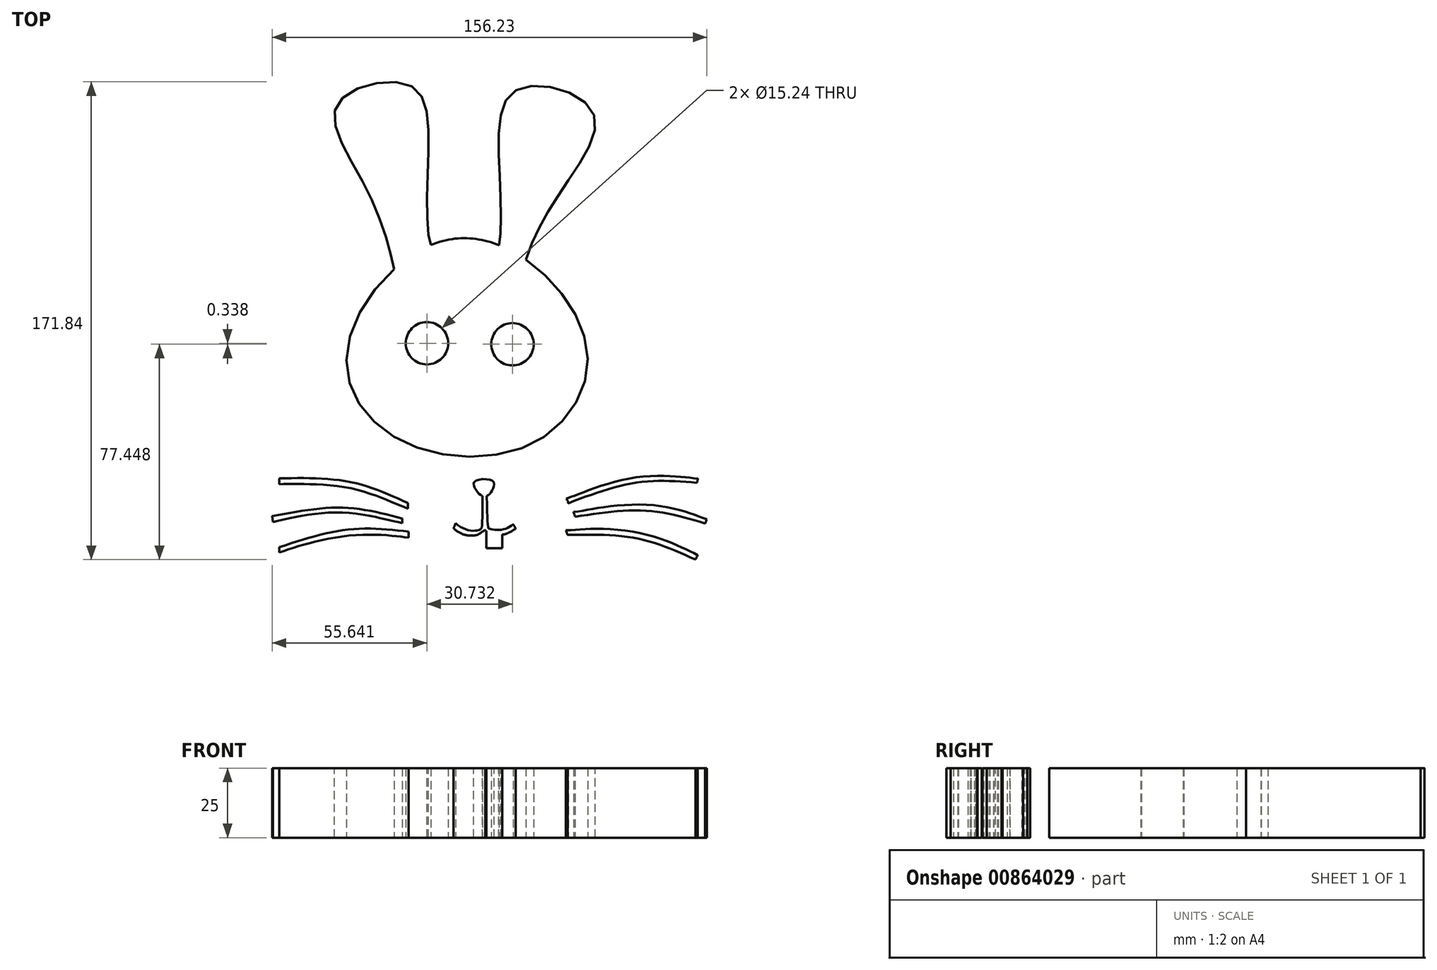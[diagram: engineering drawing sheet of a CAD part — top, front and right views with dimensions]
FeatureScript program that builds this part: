
annotation { "Feature Type Name" : "Feature", "Feature Type Description" : "" }
export const myFeature = defineFeature(function(context is Context, id is Id, definition is map)
    precondition{}
    {
        {
            var Q0;
            Q0=qCreatedBy(makeId("Top.planeOp"),FACE);
            var sketch = newSketch(context, id + "F0", { "sketchPlane" : qUnion([Q0])});
            skFitSpline(sketch, "E0", {"points": [v(-36.2, 9.29) * mm, v(12.18, 7.82) * mm, v(31.91, 39.07) * mm, v(9.73, 73.68) * mm, v(-24.49, 79.1) * mm, v(-54.7, 41.08) * mm, v(-36.2, 9.29) * mm]});
            skFitSpline(sketch, "E1", {"points": [v(-37.74, 70.4) * mm, v(-48.46, 100.88) * mm, v(-58.06, 129.69) * mm, v(-31.96, 136.42) * mm, v(-25.5, 110.88) * mm, v(-24.49, 79.1) * mm], "startDerivative": vector(-22.6, 116.84) * mm, "endDerivative": vector(28.19, -55.26) * mm});
            skFitSpline(sketch, "E2", {"points": [v(0, 79.03) * mm, v(0, 109.9) * mm, v(6.86, 135.17) * mm, v(33.5, 127.3) * mm, v(23.98, 100.93) * mm, v(9.64, 73.75) * mm], "startDerivative": vector(17.2, 73.4) * mm, "endDerivative": vector(-45.43, -142.03) * mm});
            skCircle(sketch, "E3", {"center": v(4.82, 43.4) * mm, "radius": 7.62 * mm});
            skFitSpline(sketch, "E4", {"points": [v(-8.66, -5.94) * mm, v(-2.18, -5.86) * mm, v(-2.23, -8.65) * mm, v(-4.07, -11.03) * mm, v(-5.95, -11.19) * mm, v(-8.38, -8.9) * mm, v(-8.66, -5.94) * mm]});
            skFitSpline(sketch, "E5", {"points": [v(-32.76, -13.72) * mm, v(-53.34, -6.18) * mm, v(-79.02, -4.8) * mm], "startDerivative": vector(-41.24, 18.8) * mm, "endDerivative": vector(-50.55, -0.73) * mm});
            skFitSpline(sketch, "E6", {"points": [v(-34.75, -19.24) * mm, v(-56.32, -15.39) * mm, v(-81.55, -18.44) * mm], "startDerivative": vector(-43.88, 11.36) * mm, "endDerivative": vector(-49.66, -9.5) * mm});
            skFitSpline(sketch, "E7", {"points": [v(-32.48, -23.98) * mm, v(-54.4, -23.27) * mm, v(-78.94, -29.63) * mm], "startDerivative": vector(-45.02, 5.21) * mm, "endDerivative": vector(-47.88, -16.24) * mm});
            skFitSpline(sketch, "E8", {"points": [v(71.13, -6.42) * mm, v(49.21, -6.38) * mm, v(24.9, -13.78) * mm], "startDerivative": vector(-45.18, 3.54) * mm, "endDerivative": vector(-47.24, -18) * mm});
            skFitSpline(sketch, "E9", {"points": [v(-6.01, -11.16) * mm, v(-6.11, -21.85) * mm, v(-6.65, -23.12) * mm, v(-7.96, -23.58) * mm, v(-11.86, -23.2) * mm, v(-15.6, -21) * mm], "startDerivative": vector(0.56, 10.66) * mm, "endDerivative": vector(-7.08, 7.75) * mm});
            skFitSpline(sketch, "E10", {"points": [v(-4.5, -11.23) * mm, v(-4.01, -21.8) * mm, v(-3.42, -22.97) * mm, v(0.35, -23.35) * mm, v(5.06, -21.29) * mm], "startDerivative": vector(0.53, 19.48) * mm, "endDerivative": vector(13.2, 13.76) * mm});
            skFitSpline(sketch, "E11", {"points": [v(-16.34, -22.82) * mm, v(-14.36, -24.24) * mm, v(-11.92, -25.24) * mm, v(-7.73, -25.09) * mm, v(-5.4, -23.62) * mm, v(-4.84, -23.5) * mm], "startDerivative": vector(2.92, -3.81) * mm, "endDerivative": vector(0.02, 0) * mm});
            skFitSpline(sketch, "E12", {"points": [v(-16.34, -22.82) * mm, v(-15.6, -21) * mm], "startDerivative": vector(0.22, 0.2) * mm, "endDerivative": vector(0.22, 0.2) * mm});
            skFitSpline(sketch, "E13", {"points": [v(5.96, -22.78) * mm, v(4.26, -24) * mm, v(2.76, -24.7) * mm, v(0.66, -25.05) * mm, v(-4.9, -23.57) * mm, v(-4.84, -23.5) * mm], "startDerivative": vector(-4.26, -5.04) * mm, "endDerivative": vector(0.06, -0.04) * mm});
            skFitSpline(sketch, "E14", {"points": [v(5.06, -21.29) * mm, v(5.96, -22.78) * mm], "startDerivative": vector(0.26, -0.24) * mm, "endDerivative": vector(0.26, -0.24) * mm});
            skFitSpline(sketch, "E15", {"points": [v(24.9, -13.78) * mm, v(24.1, -12.13) * mm], "startDerivative": vector(-0.89, 1.21) * mm, "endDerivative": vector(-4.1, 5.36) * mm});
            skFitSpline(sketch, "E16", {"points": [v(71.52, -4.92) * mm, v(64.52, -4.2) * mm, v(49.36, -4.48) * mm, v(32.5, -9) * mm, v(24.1, -12.13) * mm], "startDerivative": vector(-35.55, 3.58) * mm, "endDerivative": vector(-37.71, -11.92) * mm});
            skFitSpline(sketch, "E17", {"points": [v(71.52, -4.92) * mm, v(71.13, -6.42) * mm], "startDerivative": vector(-0.37, -1.3) * mm, "endDerivative": vector(-0.37, -1.3) * mm});
            skFitSpline(sketch, "E18", {"points": [v(74.11, -21.05) * mm, v(52.68, -16.45) * mm, v(27.37, -18.63) * mm], "startDerivative": vector(-43.46, 12.87) * mm, "endDerivative": vector(-49.95, -7.77) * mm});
            skFitSpline(sketch, "E19", {"points": [v(74.68, -19.54) * mm, v(67.69, -17.02) * mm, v(52.89, -14.3) * mm, v(35.4, -15.52) * mm, v(26.77, -16.92) * mm], "startDerivative": vector(-34.03, 10.9) * mm, "endDerivative": vector(-39.31, -4.15) * mm});
            skFitSpline(sketch, "E20", {"points": [v(74.68, -19.54) * mm, v(74.11, -21.05) * mm], "startDerivative": vector(-0.64, -1.2) * mm, "endDerivative": vector(-0.64, -1.2) * mm});
            skFitSpline(sketch, "E21", {"points": [v(26.77, -16.92) * mm, v(27.37, -18.63) * mm], "startDerivative": vector(0.53, -1.44) * mm, "endDerivative": vector(0.53, -1.44) * mm});
            skFitSpline(sketch, "E22", {"points": [v(70.57, -34.05) * mm, v(49.99, -26.51) * mm, v(24.61, -25.16) * mm], "startDerivative": vector(-41.25, 18.78) * mm, "endDerivative": vector(-50.55, -0.76) * mm});
            skFitSpline(sketch, "E23", {"points": [v(71.44, -32.47) * mm, v(64.86, -29.26) * mm, v(50.63, -24.5) * mm, v(32.86, -23.01) * mm, v(24.06, -23.42) * mm], "startDerivative": vector(-32.19, 15.52) * mm, "endDerivative": vector(-39.54, 1.26) * mm});
            skFitSpline(sketch, "E24", {"points": [v(71.44, -32.47) * mm, v(70.57, -34.05) * mm], "startDerivative": vector(-0.8, -1.1) * mm, "endDerivative": vector(-0.8, -1.1) * mm});
            skFitSpline(sketch, "E25", {"points": [v(24.06, -23.42) * mm, v(24.61, -25.16) * mm], "startDerivative": vector(0.33, -1.5) * mm, "endDerivative": vector(0.33, -1.5) * mm});
            skFitSpline(sketch, "E26", {"points": [v(-79.02, -6.9) * mm, v(-69.9, -6.89) * mm, v(-53.18, -8.43) * mm, v(-39.72, -12.85) * mm, v(-32.76, -15.73) * mm], "startDerivative": vector(36.66, 1.52) * mm, "endDerivative": vector(31.86, -13.34) * mm});
            skFitSpline(sketch, "E27", {"points": [v(-79.02, -4.8) * mm, v(-79.02, -6.9) * mm], "startDerivative": vector(0, -2.27) * mm, "endDerivative": vector(0, -2.27) * mm});
            skFitSpline(sketch, "E28", {"points": [v(-32.76, -13.72) * mm, v(-32.76, -15.73) * mm], "startDerivative": vector(0, -2) * mm, "endDerivative": vector(0, -2) * mm});
            skFitSpline(sketch, "E29", {"points": [v(-81.26, -20.52) * mm, v(-72.7, -18.62) * mm, v(-56.66, -17.12) * mm, v(-41.84, -19.3) * mm, v(-34.77, -20.93) * mm], "startDerivative": vector(35.86, 8.75) * mm, "endDerivative": vector(32.29, -7.65) * mm});
            skFitSpline(sketch, "E30", {"points": [v(-81.55, -18.44) * mm, v(-81.26, -20.52) * mm], "startDerivative": vector(0.3, -2.08) * mm, "endDerivative": vector(0.3, -2.08) * mm});
            skFitSpline(sketch, "E31", {"points": [v(-34.75, -19.24) * mm, v(-34.77, -20.93) * mm], "startDerivative": vector(-0.02, -1.68) * mm, "endDerivative": vector(-0.02, -1.68) * mm});
            skFitSpline(sketch, "E32", {"points": [v(-78.94, -31.5) * mm, v(-69.55, -28.5) * mm, v(-53.51, -25.38) * mm, v(-39.37, -25.38) * mm, v(-32.44, -26.2) * mm], "startDerivative": vector(37.6, 12.9) * mm, "endDerivative": vector(32.58, -4.56) * mm});
            skFitSpline(sketch, "E33", {"points": [v(-78.94, -29.63) * mm, v(-78.94, -31.5) * mm], "startDerivative": vector(0, -1.87) * mm, "endDerivative": vector(0, -1.87) * mm});
            skFitSpline(sketch, "E34", {"points": [v(-32.48, -23.98) * mm, v(-32.44, -26.2) * mm], "startDerivative": vector(0.03, -2.2) * mm, "endDerivative": vector(0.03, -2.2) * mm});
            skLineSegment(sketch, "E35", {"start": v(-10.92, -25.4) * mm, "end": v(-10.92, -29.79) * mm});
            skLineSegment(sketch, "E36", {"start": v(-10.92, -29.79) * mm, "end": v(-5.05, -29.79) * mm});
            skLineSegment(sketch, "E37", {"start": v(-4.84, -23.5) * mm, "end": v(-4.84, -29.79) * mm});
            skLineSegment(sketch, "E38", {"start": v(-4.54, -23.82) * mm, "end": v(-4.54, -29.97) * mm});
            skLineSegment(sketch, "E39", {"start": v(-4.54, -29.97) * mm, "end": v(1.13, -29.97) * mm});
            skLineSegment(sketch, "E40", {"start": v(1.13, -29.97) * mm, "end": v(1.13, -25.07) * mm});
            skCircle(sketch, "E41", {"center": v(-25.9, 43.74) * mm, "radius": 7.62 * mm});
            skSolve(sketch);
        }
        {
            var Q0;
            Q0 = qSketchRegion(id + "F0", true);
            extrude(context, id + "F1", {"entities" : qUnion([Q0]), "depth" : 25 * mm, "offsetDistance" : 25 * mm});
        }
    });
